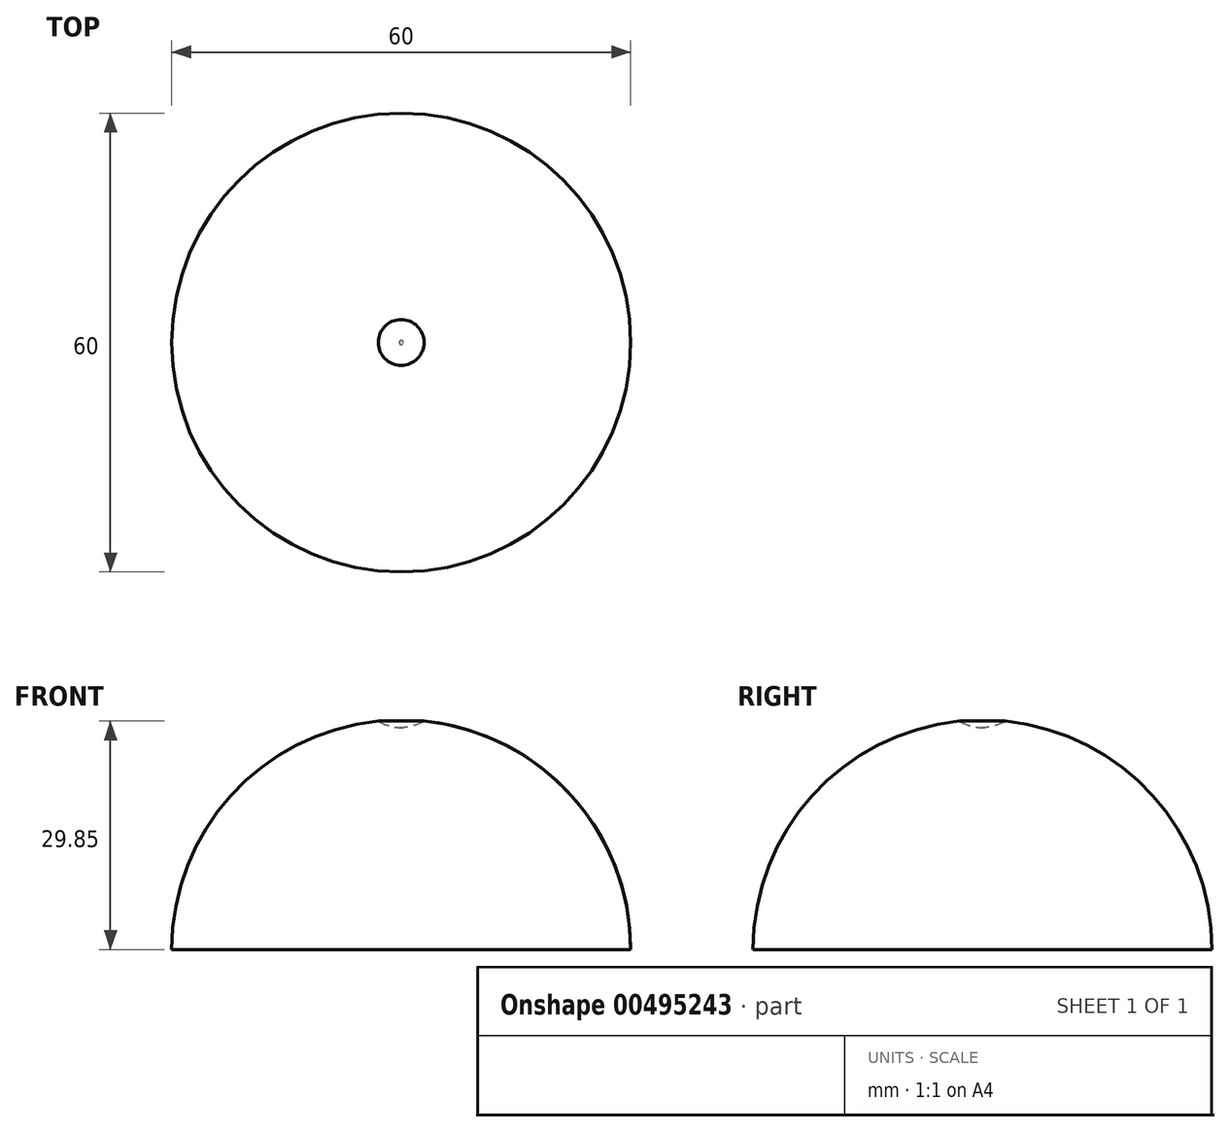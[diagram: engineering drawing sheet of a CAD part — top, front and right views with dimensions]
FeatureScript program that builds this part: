
annotation { "Feature Type Name" : "Feature", "Feature Type Description" : "" }
export const myFeature = defineFeature(function(context is Context, id is Id, definition is map)
    precondition{}
    {
        {
            var Q0;
            Q0=qCreatedBy(makeId("Front.planeOp"),FACE);
            var sketch = newSketch(context, id + "F0", { "sketchPlane" : qUnion([Q0])});
            skArc(sketch, "E0", {"start": v(30, 0) * mm, "mid": v(21.21, 21.21) * mm, "end": v(0, 30) * mm});
            skLineSegment(sketch, "E1", {"start": v(0, 30) * mm, "end": v(0, 0) * mm});
            skLineSegment(sketch, "E2", {"start": v(0, 0) * mm, "end": v(30, 0) * mm});
            skSolve(sketch);
        }
        {
            var Q0;
            Q0=makeQuery(id+"F0.imprint","IMPRINT",FACE,{"disambiguationData":[TD([[makeQuery(id+"F0.imprint","IMPRINT",EDGE,{"derivedFrom":sQuery(id+"F0.wireOp",EDGE,"E0")}),1.0]])]});
            var Q1;
            Q1=sQuery(id+"F0.wireOp",EDGE,"E1");
            revolve(context, id + "F1", {"entities" : qUnion([Q0]), "axis" : qUnion([Q1]), "revolveType" : RevolveType.FULL});
        }
        {
            var Q0;
            Q0=qCreatedBy(makeId("Front.planeOp"),FACE);
            var sketch = newSketch(context, id + "F2", { "sketchPlane" : qUnion([Q0])});
            skArc(sketch, "E3", {"start": v(30, 0) * mm, "mid": v(0, 30) * mm, "end": v(-30, 0) * mm});
            skArc(sketch, "E4", {"start": v(3, 29.85) * mm, "mid": v(1.5, 29.96) * mm, "end": v(0, 30) * mm});
            skArc(sketch, "E5", {"start": v(0, 29) * mm, "mid": v(1.55, 29.23) * mm, "end": v(3, 29.85) * mm});
            skLineSegment(sketch, "E6", {"start": v(0, 29) * mm, "end": v(0, 30) * mm});
            skSolve(sketch);
        }
        {
            var Q0;
            Q0 = qSketchRegion(id + "F2", true);
            var Q1;
            Q1=sQuery(id+"F2.wireOp",EDGE,"E6");
            revolve(context, id + "F3", {"operationType" : NewBodyOperationType.REMOVE, "entities" : qUnion([Q0]), "axis" : qUnion([Q1]), "revolveType" : RevolveType.FULL, "oppositeDirection" : true});
        }
    });
